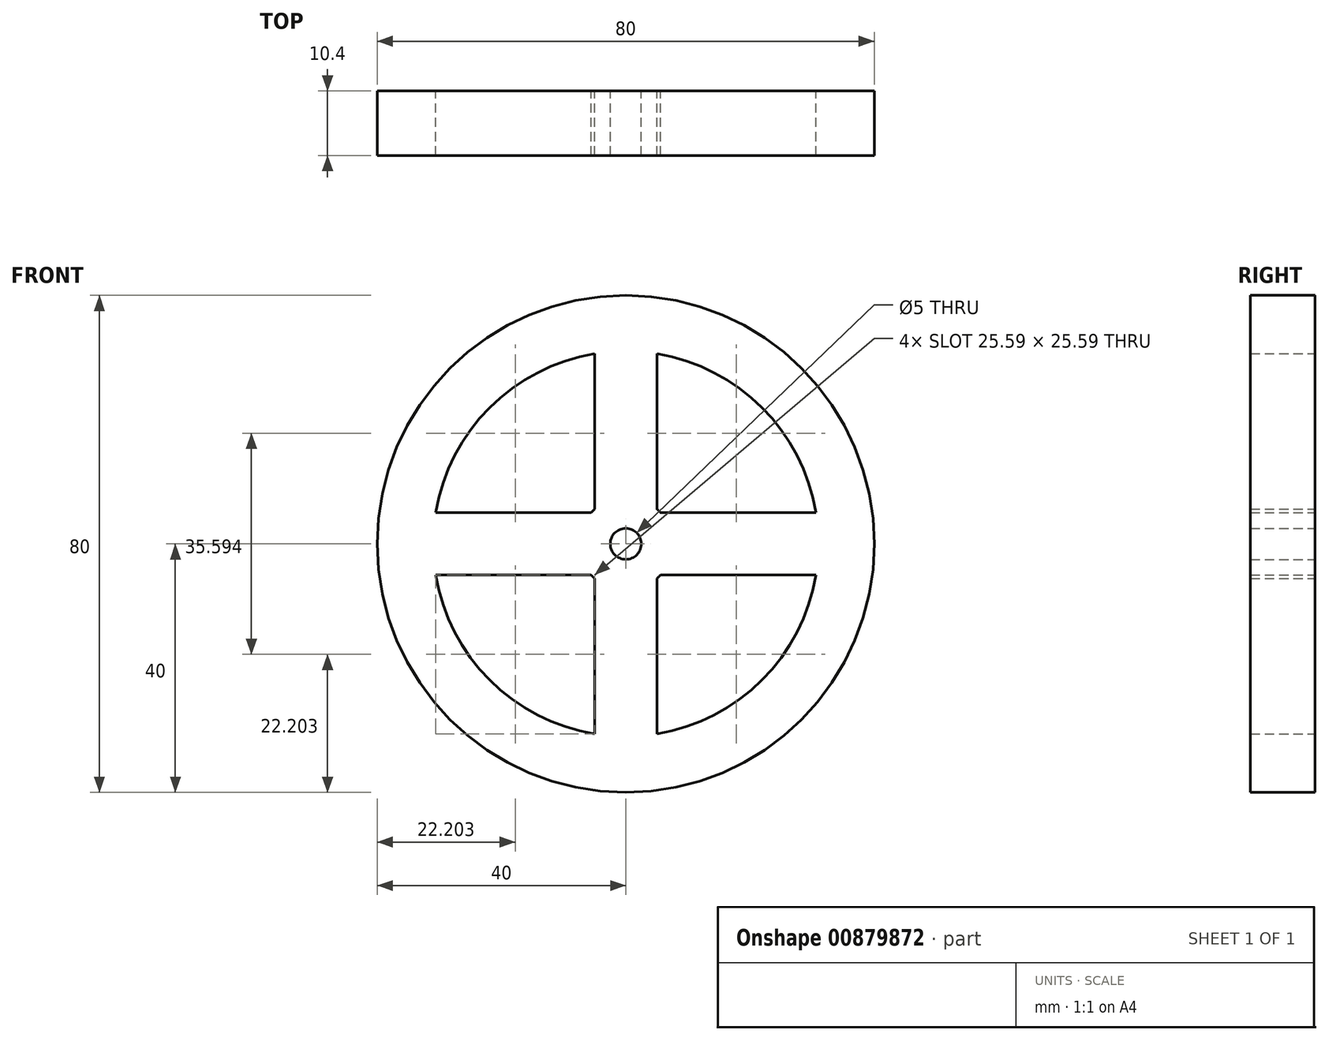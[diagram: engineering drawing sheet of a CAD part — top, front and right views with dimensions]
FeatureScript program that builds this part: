
annotation { "Feature Type Name" : "Feature", "Feature Type Description" : "" }
export const myFeature = defineFeature(function(context is Context, id is Id, definition is map)
    precondition{}
    {
        {
            var Q0;
            Q0=qCreatedBy(makeId("Front.planeOp"),FACE);
            var sketch = newSketch(context, id + "F0", { "sketchPlane" : qUnion([Q0])});
            skCircle(sketch, "E0", {"center": v(0, 0) * mm, "radius": 40 * mm});
            skArc(sketch, "E1", {"start": v(-5, 30.6) * mm, "mid": v(-21.92, 21.92) * mm, "end": v(-30.6, 5) * mm});
            skArc(sketch, "E2", {"start": v(5, -5.6) * mm, "mid": v(5.3, -5.3) * mm, "end": v(5.6, -5) * mm});
            skCircle(sketch, "E3", {"center": v(0, 0) * mm, "radius": 2.5 * mm});
            skLineSegment(sketch, "E4", {"start": v(0, 0) * mm, "end": v(-31, 0) * mm});
            skLineSegment(sketch, "E5", {"start": v(0, 0) * mm, "end": v(0, 31) * mm});
            skLineSegment(sketch, "E6", {"start": v(0, 0) * mm, "end": v(31, 0) * mm});
            skLineSegment(sketch, "E7", {"start": v(31, 0) * mm, "end": v(0, 0) * mm});
            skLineSegment(sketch, "E8", {"start": v(0, 0) * mm, "end": v(0, -31) * mm});
            skLineSegment(sketch, "E9.0", {"start": v(-5, 5.6) * mm, "end": v(-5, 30.6) * mm});
            skLineSegment(sketch, "E10.0", {"start": v(30.6, -5) * mm, "end": v(5.6, -5) * mm});
            skLineSegment(sketch, "E11.0", {"start": v(30.6, 5) * mm, "end": v(5.6, 5) * mm});
            skLineSegment(sketch, "E12.0", {"start": v(-5, -5.6) * mm, "end": v(-5, -30.6) * mm});
            skLineSegment(sketch, "E13.0", {"start": v(5, -5.6) * mm, "end": v(5, -30.6) * mm});
            skLineSegment(sketch, "E14.0", {"start": v(-5.6, 5) * mm, "end": v(-30.6, 5) * mm});
            skLineSegment(sketch, "E15.0", {"start": v(-5.6, -5) * mm, "end": v(-30.6, -5) * mm});
            skArc(sketch, "E16.trimOffspring", {"start": v(30.6, 5) * mm, "mid": v(21.92, 21.92) * mm, "end": v(5, 30.6) * mm});
            skArc(sketch, "E17.trimOffspring", {"start": v(-30.6, -5) * mm, "mid": v(-21.92, -21.92) * mm, "end": v(-5, -30.6) * mm});
            skArc(sketch, "E18.trimOffspring", {"start": v(5, -30.6) * mm, "mid": v(21.92, -21.92) * mm, "end": v(30.6, -5) * mm});
            skArc(sketch, "E19.trimOffspring", {"start": v(5.6, 5) * mm, "mid": v(5.3, 5.3) * mm, "end": v(5, 5.6) * mm});
            skArc(sketch, "E20.trimOffspring", {"start": v(-5.6, -5) * mm, "mid": v(-5.3, -5.3) * mm, "end": v(-5, -5.6) * mm});
            skArc(sketch, "E21.trimOffspring", {"start": v(-5, 5.6) * mm, "mid": v(-5.3, 5.3) * mm, "end": v(-5.6, 5) * mm});
            skLineSegment(sketch, "E22.trimOffspring", {"start": v(5, 5.6) * mm, "end": v(5, 30.6) * mm});
            skSolve(sketch);
        }
        {
            var Q0;
            Q0 = qSketchRegion(id + "F0", true);
            extrude(context, id + "F1", {"entities" : qUnion([Q0]), "depth" : 10.4 * mm, "offsetDistance" : 25 * mm});
        }
    });
